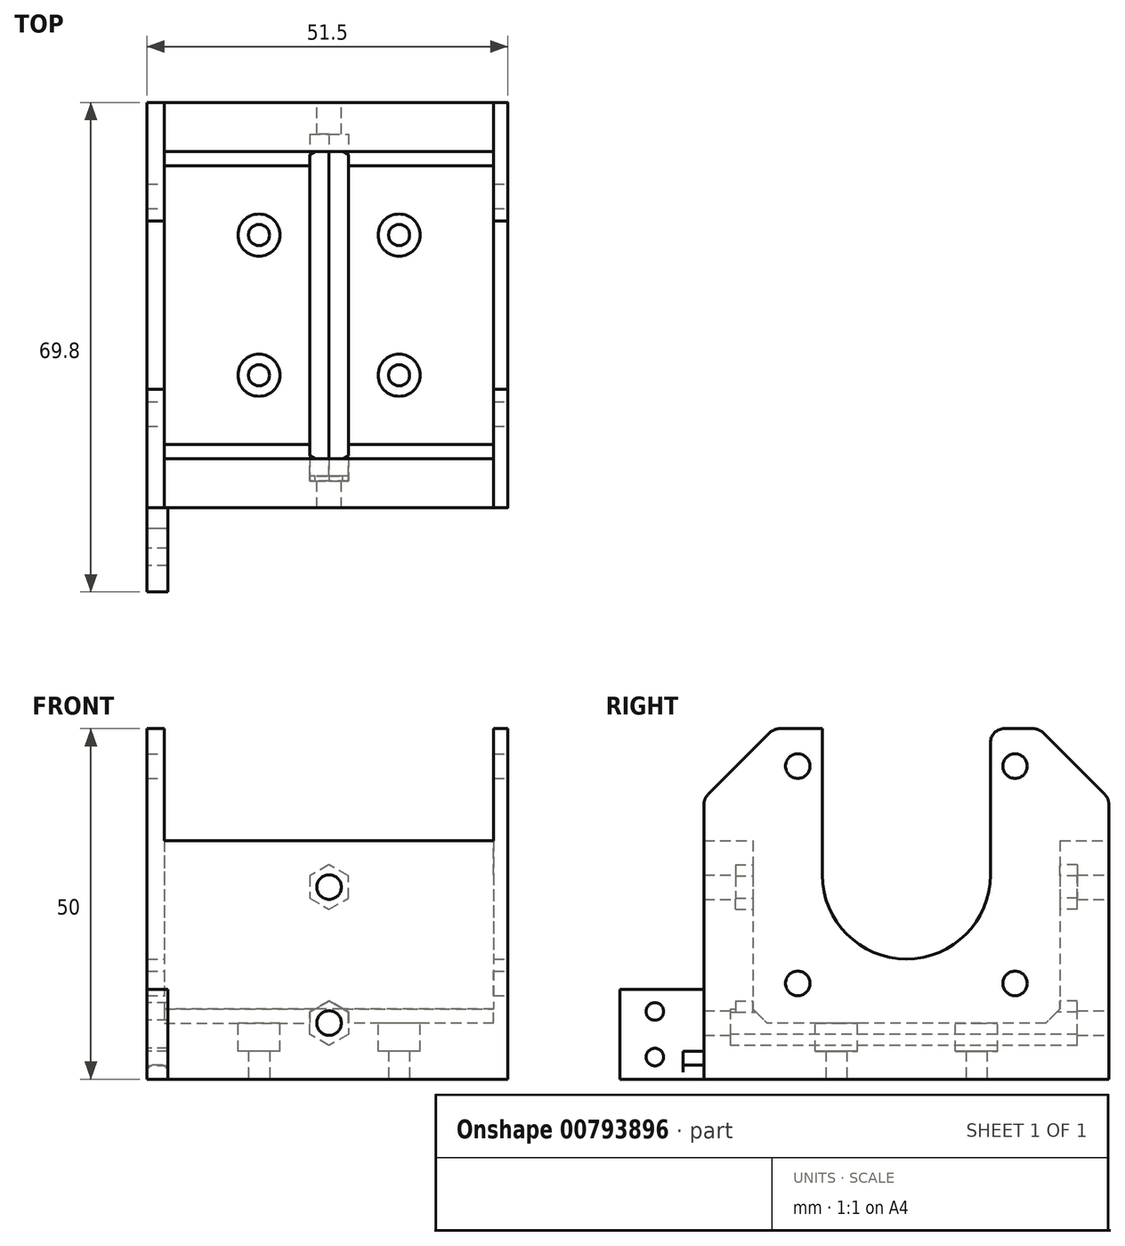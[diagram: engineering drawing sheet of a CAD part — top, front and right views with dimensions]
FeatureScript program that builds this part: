
annotation { "Feature Type Name" : "Feature", "Feature Type Description" : "" }
export const myFeature = defineFeature(function(context is Context, id is Id, definition is map)
    precondition{}
    {
        {
            var Q0;
            Q0=qCreatedBy(makeId("Top.planeOp"),FACE);
            var sketch = newSketch(context, id + "F0", { "sketchPlane" : qUnion([Q0])});
            skLineSegment(sketch, "E0.bottom", {"start": v(-13.5, 21.9) * mm, "end": v(13.5, 21.9) * mm, "construction": true});
            skLineSegment(sketch, "E0.top", {"start": v(-13.5, -21.9) * mm, "end": v(13.5, -21.9) * mm, "construction": true});
            skLineSegment(sketch, "E0.left", {"start": v(-13.5, 21.9) * mm, "end": v(-13.5, -21.9) * mm, "construction": true});
            skLineSegment(sketch, "E0.right", {"start": v(13.5, 21.9) * mm, "end": v(13.5, -21.9) * mm, "construction": true});
            skCircle(sketch, "E1", {"center": v(-10, 10) * mm, "radius": 1.5 * mm, "construction": true});
            skCircle(sketch, "E2", {"center": v(10, 10) * mm, "radius": 1.5 * mm, "construction": true});
            skCircle(sketch, "E3", {"center": v(10, -10) * mm, "radius": 1.5 * mm, "construction": true});
            skCircle(sketch, "E4", {"center": v(-10, -10) * mm, "radius": 1.5 * mm, "construction": true});
            skSolve(sketch);
        }
        {
            var Q0;
            Q0=qCreatedBy(makeId("Top.planeOp"),FACE);
            var sketch = newSketch(context, id + "F1", { "sketchPlane" : qUnion([Q0])});
            skLineSegment(sketch, "E5.0", {"start": v(-13.5, 21.9) * mm, "end": v(-13.5, -21.9) * mm});
            skLineSegment(sketch, "E6.0", {"start": v(-13.5, 21.9) * mm, "end": v(13.5, 21.9) * mm});
            skLineSegment(sketch, "E7.0", {"start": v(13.5, 21.9) * mm, "end": v(13.5, -21.9) * mm});
            skLineSegment(sketch, "E8.0", {"start": v(-13.5, -21.9) * mm, "end": v(13.5, -21.9) * mm});
            skPoint(sketch, "E9.0", {"position": v(-10, -10) * mm});
            skPoint(sketch, "E10.0", {"position": v(10, -10) * mm});
            skPoint(sketch, "E11.0", {"position": v(10, 10) * mm});
            skCircle(sketch, "E12.0", {"center": v(-10, -10) * mm, "radius": 1.5 * mm});
            skCircle(sketch, "E13.0", {"center": v(10, -10) * mm, "radius": 1.5 * mm});
            skCircle(sketch, "E14.0", {"center": v(10, 10) * mm, "radius": 1.5 * mm});
            skCircle(sketch, "E15.0", {"center": v(-10, 10) * mm, "radius": 1.5 * mm});
            skLineSegment(sketch, "E16.top", {"start": v(-13.5, -28.9) * mm, "end": v(13.5, -28.9) * mm});
            skLineSegment(sketch, "E16.left", {"start": v(-13.5, -21.9) * mm, "end": v(-13.5, -28.9) * mm});
            skLineSegment(sketch, "E16.right", {"start": v(13.5, -21.9) * mm, "end": v(13.5, -28.9) * mm});
            skLineSegment(sketch, "E17.top", {"start": v(-13.5, 28.9) * mm, "end": v(13.5, 28.9) * mm});
            skLineSegment(sketch, "E17.left", {"start": v(-13.5, 21.9) * mm, "end": v(-13.5, 28.9) * mm});
            skLineSegment(sketch, "E17.right", {"start": v(13.5, 21.9) * mm, "end": v(13.5, 28.9) * mm});
            skSolve(sketch);
        }
        {
            var Q0;
            Q0=qSketchRegion(id+"F1",true);
            extrude(context, id + "F2", {"entities" : qUnion([Q0]), "depth" : 34 * mm, "offsetDistance" : 25 * mm});
        }
        {
            var Q0;
            Q0=makeQuery(id+"F2.opExtrude","SWEPT_FACE",FACE,{"disambiguationData":[OSD([sQuery(id+"F1.wireOp",EDGE,"E17.top")])]});
            var sketch = newSketch(context, id + "F3", { "sketchPlane" : qUnion([Q0])});
            skCircle(sketch, "E18", {"center": v(0, 27.4) * mm, "radius": 1.75 * mm});
            skCircle(sketch, "E19", {"center": v(0, 8) * mm, "radius": 1.75 * mm});
            skSolve(sketch);
        }
        {
            var Q0;
            Q0=qSketchRegion(id+"F3",true);
            extrude(context, id + "F4", {"entities" : qUnion([Q0]), "operationType" : NewBodyOperationType.REMOVE, "endBound" : BoundingType.THROUGH_ALL, "oppositeDirection" : true, "depth" : 25 * mm, "offsetDistance" : 25 * mm});
        }
        {
            var Q0;
            Q0=makeQuery(id+"F2.opExtrude","SWEPT_FACE",FACE,{"disambiguationData":[OSD([sQuery(id+"F1.wireOp",EDGE,"E5.0"),sQuery(id+"F1.wireOp",EDGE,"E16.left"),sQuery(id+"F1.wireOp",EDGE,"E17.left")])]});
            var sketch = newSketch(context, id + "F5", { "sketchPlane" : qUnion([Q0])});
            skLineSegment(sketch, "E20.bottom", {"start": v(-21.9, 34) * mm, "end": v(21.9, 34) * mm});
            skLineSegment(sketch, "E20.top", {"start": v(-21.9, 8) * mm, "end": v(21.9, 8) * mm});
            skLineSegment(sketch, "E20.left", {"start": v(-21.9, 34) * mm, "end": v(-21.9, 8) * mm});
            skLineSegment(sketch, "E20.right", {"start": v(21.9, 34) * mm, "end": v(21.9, 8) * mm});
            skSolve(sketch);
        }
        {
            var Q0;
            Q0=qSketchRegion(id+"F5",true);
            extrude(context, id + "F6", {"entities" : qUnion([Q0]), "operationType" : NewBodyOperationType.REMOVE, "endBound" : BoundingType.THROUGH_ALL, "oppositeDirection" : true, "depth" : 25 * mm, "offsetDistance" : 25 * mm});
        }
        {
            var Q0;
            Q0=makeQuery(id+"F2.opExtrude","SWEPT_FACE",FACE,{"disambiguationData":[OSD([sQuery(id+"F1.wireOp",EDGE,"E5.0"),sQuery(id+"F1.wireOp",EDGE,"E16.left"),sQuery(id+"F1.wireOp",EDGE,"E17.left")])]});
            extrude(context, id + "F7", {"entities" : qUnion([Q0]), "operationType" : NewBodyOperationType.ADD, "depth" : 10 * mm, "offsetDistance" : 25 * mm});
        }
        {
            var Q0;
            Q0=makeQuery(id+"F2.opExtrude","SWEPT_FACE",FACE,{"disambiguationData":[OSD([sQuery(id+"F1.wireOp",EDGE,"E7.0"),sQuery(id+"F1.wireOp",EDGE,"E16.right"),sQuery(id+"F1.wireOp",EDGE,"E17.right")])]});
            extrude(context, id + "F8", {"entities" : qUnion([Q0]), "operationType" : NewBodyOperationType.ADD, "depth" : 10 * mm, "offsetDistance" : 25 * mm});
        }
        {
            var Q0;
            {var subQ0=sQuery(id+"F5.wireOp",EDGE,"E20.right");var subQ1=sQuery(id+"F5.wireOp",EDGE,"E20.top");Q0=makeQuery(id+"F8.boolean.opBoolean","MERGE",EDGE,{"derivedFrom":[makeQuery(id+"F7.boolean.opBoolean","MERGE",EDGE,{"derivedFrom":[makeQuery(id+"F6.boolean.opBoolean","COPY",EDGE,{"derivedFrom":makeQuery(id+"F6.opExtrude","SWEPT_EDGE",EDGE,{"disambiguationData":[OSD([subQ1,subQ0])]})}),makeQuery(id+"F7.opExtrude","SWEPT_EDGE",EDGE,{"disambiguationData":[OSD([subQ1,subQ0])]})]}),makeQuery(id+"F8.opExtrude","SWEPT_EDGE",EDGE,{"disambiguationData":[OSD([sQuery(id+"F1.wireOp",EDGE,"E7.0"),sQuery(id+"F1.wireOp",EDGE,"E16.right"),sQuery(id+"F1.wireOp",EDGE,"E17.right"),subQ1,subQ0])]})]});}
            var Q1;
            {var subQ0=sQuery(id+"F5.wireOp",EDGE,"E20.left");var subQ1=sQuery(id+"F5.wireOp",EDGE,"E20.top");Q1=makeQuery(id+"F8.boolean.opBoolean","MERGE",EDGE,{"derivedFrom":[makeQuery(id+"F7.boolean.opBoolean","MERGE",EDGE,{"derivedFrom":[makeQuery(id+"F6.boolean.opBoolean","COPY",EDGE,{"derivedFrom":makeQuery(id+"F6.opExtrude","SWEPT_EDGE",EDGE,{"disambiguationData":[OSD([subQ1,subQ0])]})}),makeQuery(id+"F7.opExtrude","SWEPT_EDGE",EDGE,{"disambiguationData":[OSD([subQ1,subQ0])]})]}),makeQuery(id+"F8.opExtrude","SWEPT_EDGE",EDGE,{"disambiguationData":[OSD([sQuery(id+"F1.wireOp",EDGE,"E7.0"),sQuery(id+"F1.wireOp",EDGE,"E16.right"),sQuery(id+"F1.wireOp",EDGE,"E17.right"),subQ1,subQ0])]})]});}
            chamfer(context, id + "F9", {"entities" : qUnion([Q0, Q1]), "width" : 2 * mm, "tangentPropagation" : true});
        }
        {
            var Q0;
            Q0=makeQuery(id+"F7.opExtrude","CAP_FACE",FACE,{"disambiguationData":[OSD([sQuery(id+"F1.wireOp",EDGE,"E5.0"),sQuery(id+"F1.wireOp",EDGE,"E16.left"),sQuery(id+"F1.wireOp",EDGE,"E17.left")])],"isStart":false});
            var sketch = newSketch(context, id + "F10", { "sketchPlane" : qUnion([Q0])});
            skLineSegment(sketch, "E21.0", {"start": v(-21.9, 34) * mm, "end": v(-21.9, 10) * mm});
            skLineSegment(sketch, "E22.0", {"start": v(21.9, 34) * mm, "end": v(21.9, 10) * mm});
            skSolve(sketch);
        }
        {
            var Q0;
            Q0=makeQuery(id+"F10.imprint","IMPRINT",FACE,{"disambiguationData":[TD([[makeQuery(id+"F10.imprint","IMPRINT",EDGE,{"derivedFrom":sQuery(id+"F10.wireOp",EDGE,"E21.0")}),-1.0]])]});
            var sketch = newSketch(context, id + "F11", { "sketchPlane" : qUnion([Q0])});
            skLineSegment(sketch, "E23.0", {"start": v(-28.9, 34) * mm, "end": v(-28.9, 0) * mm});
            skLineSegment(sketch, "E24.0", {"start": v(-28.9, 0) * mm, "end": v(28.9, 0) * mm});
            skLineSegment(sketch, "E25.top", {"start": v(-28.9, 50) * mm, "end": v(28.9, 50) * mm});
            skLineSegment(sketch, "E25.left", {"start": v(-28.9, 34) * mm, "end": v(-28.9, 50) * mm});
            skLineSegment(sketch, "E26", {"start": v(28.9, 50) * mm, "end": v(28.9, 0) * mm});
            skSolve(sketch);
        }
        {
            var Q0;
            Q0=qSketchRegion(id+"F11",true);
            extrude(context, id + "F12", {"entities" : qUnion([Q0]), "operationType" : NewBodyOperationType.ADD, "depth" : 2.5 * mm, "offsetDistance" : 25 * mm});
        }
        {
            var Q0;
            Q0=makeQuery(id+"F8.opExtrude","CAP_FACE",FACE,{"disambiguationData":[OSD([sQuery(id+"F1.wireOp",EDGE,"E7.0"),sQuery(id+"F1.wireOp",EDGE,"E16.right"),sQuery(id+"F1.wireOp",EDGE,"E17.right")])],"isStart":false});
            var sketch = newSketch(context, id + "F13", { "sketchPlane" : qUnion([Q0])});
            skLineSegment(sketch, "E27.0", {"start": v(-28.9, 28) * mm, "end": v(-28.9, 50) * mm});
            skLineSegment(sketch, "E28.0", {"start": v(-28.9, 50) * mm, "end": v(28.9, 50) * mm});
            skLineSegment(sketch, "E29.0", {"start": v(28.9, 28) * mm, "end": v(28.9, 50) * mm});
            skLineSegment(sketch, "E30.0", {"start": v(-28.9, 34) * mm, "end": v(-28.9, 0) * mm});
            skLineSegment(sketch, "E31.0", {"start": v(28.9, 0) * mm, "end": v(-28.9, 0) * mm});
            skLineSegment(sketch, "E32.0", {"start": v(28.9, 34) * mm, "end": v(28.9, 0) * mm});
            skSolve(sketch);
        }
        {
            var Q0;
            Q0=qSketchRegion(id+"F13",true);
            extrude(context, id + "F14", {"entities" : qUnion([Q0]), "operationType" : NewBodyOperationType.ADD, "depth" : 2 * mm, "offsetDistance" : 25 * mm});
        }
        {
            var Q0;
            Q0=makeQuery(id+"F12.opExtrude","SWEPT_EDGE",EDGE,{"disambiguationData":[OSD([sQuery(id+"F11.wireOp",EDGE,"E25.top"),sQuery(id+"F11.wireOp",EDGE,"E25.left")])]});
            var Q1;
            Q1=makeQuery(id+"F12.opExtrude","SWEPT_EDGE",EDGE,{"disambiguationData":[OSD([sQuery(id+"F11.wireOp",EDGE,"E25.top"),sQuery(id+"F11.wireOp",EDGE,"E26")])]});
            var Q2;
            Q2=makeQuery(id+"F14.opExtrude","SWEPT_EDGE",EDGE,{"disambiguationData":[OSD([sQuery(id+"F13.wireOp",EDGE,"E27.0"),sQuery(id+"F13.wireOp",EDGE,"E28.0")])]});
            var Q3;
            Q3=makeQuery(id+"F14.opExtrude","SWEPT_EDGE",EDGE,{"disambiguationData":[OSD([sQuery(id+"F13.wireOp",EDGE,"E28.0"),sQuery(id+"F13.wireOp",EDGE,"E29.0")])]});
            chamfer(context, id + "F15", {"entities" : qUnion([Q0, Q1, Q2, Q3]), "width" : 10 * mm, "tangentPropagation" : true});
        }
        {
            var Q0;
            Q0=makeQuery(id+"F14.opExtrude","CAP_FACE",FACE,{"disambiguationData":[OSD([sQuery(id+"F13.wireOp",EDGE,"E27.0"),sQuery(id+"F13.wireOp",EDGE,"E28.0"),sQuery(id+"F13.wireOp",EDGE,"E29.0"),sQuery(id+"F13.wireOp",EDGE,"E30.0"),sQuery(id+"F13.wireOp",EDGE,"E31.0"),sQuery(id+"F13.wireOp",EDGE,"E32.0")])],"isStart":false});
            var sketch = newSketch(context, id + "F16", { "sketchPlane" : qUnion([Q0])});
            skArc(sketch, "E33", {"start": v(-12, 29.15) * mm, "mid": v(0, 17.15) * mm, "end": v(12, 29.15) * mm});
            skCircle(sketch, "E34", {"center": v(-15.5, 44.65) * mm, "radius": 1.75 * mm});
            skCircle(sketch, "E35", {"center": v(15.5, 44.65) * mm, "radius": 1.75 * mm});
            skCircle(sketch, "E36", {"center": v(15.5, 13.65) * mm, "radius": 1.75 * mm});
            skCircle(sketch, "E37", {"center": v(-15.5, 13.65) * mm, "radius": 1.75 * mm});
            skLineSegment(sketch, "E38", {"start": v(-12, 29.15) * mm, "end": v(-12, 50) * mm});
            skLineSegment(sketch, "E39", {"start": v(12, 29.15) * mm, "end": v(12, 50) * mm});
            skLineSegment(sketch, "E40", {"start": v(-12, 50) * mm, "end": v(12, 50) * mm});
            skSolve(sketch);
        }
        {
            var Q0;
            Q0=qSketchRegion(id+"F16",true);
            var Q1;
            Q1=makeQuery(id+"F12.opExtrude","CAP_FACE",FACE,{"disambiguationData":[OSD([sQuery(id+"F11.wireOp",EDGE,"E23.0"),sQuery(id+"F11.wireOp",EDGE,"E24.0"),sQuery(id+"F11.wireOp",EDGE,"E25.top"),sQuery(id+"F11.wireOp",EDGE,"E25.left"),sQuery(id+"F11.wireOp",EDGE,"E26")])],"isStart":false});
            extrude(context, id + "F17", {"entities" : qUnion([Q0]), "operationType" : NewBodyOperationType.REMOVE, "endBound" : BoundingType.UP_TO_SURFACE, "oppositeDirection" : true, "depth" : 25 * mm, "endBoundEntityFace" : qUnion([Q1]), "offsetDistance" : 25 * mm});
        }
        {
            var Q0;
            {var subQ0=sQuery(id+"F5.wireOp",EDGE,"E20.top");Q0=makeQuery(id+"F8.boolean.opBoolean","MERGE",FACE,{"derivedFrom":[makeQuery(id+"F7.boolean.opBoolean","MERGE",FACE,{"derivedFrom":[makeQuery(id+"F6.boolean.opBoolean","COPY",FACE,{"derivedFrom":makeQuery(id+"F6.opExtrude","SWEPT_FACE",FACE,{"disambiguationData":[OSD([subQ0])]})}),makeQuery(id+"F7.opExtrude","SWEPT_FACE",FACE,{"disambiguationData":[OSD([subQ0])]})]}),makeQuery(id+"F8.opExtrude","SWEPT_FACE",FACE,{"disambiguationData":[OSD([sQuery(id+"F1.wireOp",EDGE,"E7.0"),sQuery(id+"F1.wireOp",EDGE,"E16.right"),sQuery(id+"F1.wireOp",EDGE,"E17.right"),subQ0])]})]});}
            var sketch = newSketch(context, id + "F18", { "sketchPlane" : qUnion([Q0])});
            skPoint(sketch, "E41", {"position": v(10, -10) * mm});
            skPoint(sketch, "E42", {"position": v(10, 10) * mm});
            skCircle(sketch, "E43", {"center": v(10, -10) * mm, "radius": 3 * mm});
            skCircle(sketch, "E44", {"center": v(10, 10) * mm, "radius": 3 * mm});
            skCircle(sketch, "E45.0", {"center": v(-10, -10) * mm, "radius": 1.5 * mm, "construction": true});
            skCircle(sketch, "E46.0", {"center": v(-10, 10) * mm, "radius": 1.5 * mm, "construction": true});
            skCircle(sketch, "E47", {"center": v(-10, -10) * mm, "radius": 3 * mm});
            skCircle(sketch, "E48", {"center": v(-10, 10) * mm, "radius": 3 * mm});
            skSolve(sketch);
        }
        {
            var Q0;
            Q0=qSketchRegion(id+"F18",true);
            extrude(context, id + "F19", {"entities" : qUnion([Q0]), "operationType" : NewBodyOperationType.REMOVE, "oppositeDirection" : true, "depth" : 4 * mm, "offsetDistance" : 25 * mm});
        }
        {
            var Q0;
            {var subQ0=sQuery(id+"F5.wireOp",EDGE,"E20.left");Q0=makeQuery(id+"F8.boolean.opBoolean","MERGE",FACE,{"derivedFrom":[makeQuery(id+"F7.boolean.opBoolean","MERGE",FACE,{"derivedFrom":[makeQuery(id+"F6.boolean.opBoolean","COPY",FACE,{"derivedFrom":makeQuery(id+"F6.opExtrude","SWEPT_FACE",FACE,{"disambiguationData":[OSD([subQ0])]})}),makeQuery(id+"F7.opExtrude","SWEPT_FACE",FACE,{"disambiguationData":[OSD([subQ0])]})]}),makeQuery(id+"F8.opExtrude","SWEPT_FACE",FACE,{"disambiguationData":[OSD([sQuery(id+"F1.wireOp",EDGE,"E7.0"),sQuery(id+"F1.wireOp",EDGE,"E16.right"),sQuery(id+"F1.wireOp",EDGE,"E17.right"),subQ0])]})]});}
            var sketch = newSketch(context, id + "F20", { "sketchPlane" : qUnion([Q0])});
            skPoint(sketch, "E49", {"position": v(0, 25.64) * mm});
            skPoint(sketch, "E50", {"position": v(0, 27.4) * mm});
            skPoint(sketch, "E51", {"position": v(0, 7.96) * mm});
            skPoint(sketch, "E51.positionSnap0", {"position": v(0, 10) * mm});
            skCircle(sketch, "E52.cCircle", {"center": v(0, 27.4) * mm, "radius": 2.75 * mm, "construction": true});
            skLineSegment(sketch, "E52.0", {"start": v(2.75, 28.98) * mm, "end": v(2.75, 25.8) * mm});
            skLineSegment(sketch, "E52.1", {"start": v(2.75, 25.8) * mm, "end": v(0, 24.22) * mm});
            skLineSegment(sketch, "E52.2", {"start": v(0, 24.22) * mm, "end": v(-2.75, 25.8) * mm});
            skLineSegment(sketch, "E52.3", {"start": v(-2.75, 25.8) * mm, "end": v(-2.75, 28.98) * mm});
            skLineSegment(sketch, "E52.4", {"start": v(-2.75, 28.98) * mm, "end": v(0, 30.57) * mm});
            skLineSegment(sketch, "E52.5", {"start": v(0, 30.57) * mm, "end": v(2.75, 28.98) * mm});
            skPoint(sketch, "E52.0.midPoint", {"position": v(2.75, 27.4) * mm});
            skCircle(sketch, "E53.cCircle", {"center": v(0, 7.96) * mm, "radius": 2.75 * mm, "construction": true});
            skLineSegment(sketch, "E53.0", {"start": v(2.75, 9.55) * mm, "end": v(2.75, 6.38) * mm});
            skLineSegment(sketch, "E53.1", {"start": v(2.75, 6.38) * mm, "end": v(0, 4.79) * mm});
            skLineSegment(sketch, "E53.2", {"start": v(0, 4.79) * mm, "end": v(-2.75, 6.38) * mm});
            skLineSegment(sketch, "E53.3", {"start": v(-2.75, 6.38) * mm, "end": v(-2.75, 9.55) * mm});
            skLineSegment(sketch, "E53.4", {"start": v(-2.75, 9.55) * mm, "end": v(0, 11.14) * mm});
            skLineSegment(sketch, "E53.5", {"start": v(0, 11.14) * mm, "end": v(2.75, 9.55) * mm});
            skPoint(sketch, "E53.0.midPoint", {"position": v(2.75, 7.96) * mm});
            skSolve(sketch);
        }
        {
            var Q0;
            Q0=qSketchRegion(id+"F20",true);
            extrude(context, id + "F21", {"entities" : qUnion([Q0]), "operationType" : NewBodyOperationType.REMOVE, "oppositeDirection" : true, "depth" : 2.5 * mm, "offsetDistance" : 25 * mm});
        }
        {
            var Q0;
            {var subQ12=sQuery(id+"F20.wireOp",EDGE,"E53.0");Q0=makeQuery(id+"F20.imprint","IMPRINT",FACE,{"disambiguationData":[TD([[makeQuery(id+"F20.imprint","IMPRINT",EDGE,{"derivedFrom":subQ12}),-1.0]])]});}
            extrude(context, id + "F22", {"entities" : qUnion([Q0]), "operationType" : NewBodyOperationType.REMOVE, "depth" : 47 * mm, "offsetDistance" : 25 * mm});
        }
        {
            var Q0;
            {var subQ0=sQuery(id+"F5.wireOp",EDGE,"E20.right");Q0=makeQuery(id+"F8.boolean.opBoolean","MERGE",FACE,{"derivedFrom":[makeQuery(id+"F7.boolean.opBoolean","MERGE",FACE,{"derivedFrom":[makeQuery(id+"F6.boolean.opBoolean","COPY",FACE,{"derivedFrom":makeQuery(id+"F6.opExtrude","SWEPT_FACE",FACE,{"disambiguationData":[OSD([subQ0])]})}),makeQuery(id+"F7.opExtrude","SWEPT_FACE",FACE,{"disambiguationData":[OSD([subQ0])]})]}),makeQuery(id+"F8.opExtrude","SWEPT_FACE",FACE,{"disambiguationData":[OSD([sQuery(id+"F1.wireOp",EDGE,"E7.0"),sQuery(id+"F1.wireOp",EDGE,"E16.right"),sQuery(id+"F1.wireOp",EDGE,"E17.right"),subQ0])]})]});}
            var sketch = newSketch(context, id + "F23", { "sketchPlane" : qUnion([Q0])});
            skCircle(sketch, "E54.0", {"center": v(0, 27.4) * mm, "radius": 1.75 * mm, "construction": true});
            skCircle(sketch, "E55.0", {"center": v(0, 8) * mm, "radius": 1.75 * mm, "construction": true});
            skCircle(sketch, "E56.cCircle", {"center": v(0, 27.4) * mm, "radius": 2.75 * mm, "construction": true});
            skLineSegment(sketch, "E56.0", {"start": v(2.75, 28.98) * mm, "end": v(2.75, 25.8) * mm});
            skLineSegment(sketch, "E56.1", {"start": v(2.75, 25.8) * mm, "end": v(0, 24.22) * mm});
            skLineSegment(sketch, "E56.2", {"start": v(0, 24.22) * mm, "end": v(-2.75, 25.8) * mm});
            skLineSegment(sketch, "E56.3", {"start": v(-2.75, 25.8) * mm, "end": v(-2.75, 28.98) * mm});
            skLineSegment(sketch, "E56.4", {"start": v(-2.75, 28.98) * mm, "end": v(0, 30.57) * mm});
            skLineSegment(sketch, "E56.5", {"start": v(0, 30.57) * mm, "end": v(2.75, 28.98) * mm});
            skPoint(sketch, "E56.0.midPoint", {"position": v(2.75, 27.4) * mm});
            skCircle(sketch, "E57.cCircle", {"center": v(0, 8) * mm, "radius": 2.75 * mm, "construction": true});
            skLineSegment(sketch, "E57.0", {"start": v(2.75, 9.59) * mm, "end": v(2.75, 6.41) * mm});
            skLineSegment(sketch, "E57.1", {"start": v(2.75, 6.41) * mm, "end": v(0, 4.82) * mm});
            skLineSegment(sketch, "E57.2", {"start": v(0, 4.82) * mm, "end": v(-2.75, 6.41) * mm});
            skLineSegment(sketch, "E57.3", {"start": v(-2.75, 6.41) * mm, "end": v(-2.75, 9.59) * mm});
            skLineSegment(sketch, "E57.4", {"start": v(-2.75, 9.59) * mm, "end": v(0, 11.18) * mm});
            skLineSegment(sketch, "E57.5", {"start": v(0, 11.18) * mm, "end": v(2.75, 9.59) * mm});
            skPoint(sketch, "E57.0.midPoint", {"position": v(2.75, 8) * mm});
            skSolve(sketch);
        }
        {
            var Q0;
            Q0=qSketchRegion(id+"F23",true);
            extrude(context, id + "F24", {"entities" : qUnion([Q0]), "operationType" : NewBodyOperationType.REMOVE, "oppositeDirection" : true, "depth" : 2.5 * mm, "offsetDistance" : 25 * mm});
        }
        {
            var Q0;
            Q0=makeQuery(id+"F12.opExtrude","CAP_FACE",FACE,{"disambiguationData":[OSD([sQuery(id+"F11.wireOp",EDGE,"E23.0"),sQuery(id+"F11.wireOp",EDGE,"E24.0"),sQuery(id+"F11.wireOp",EDGE,"E25.top"),sQuery(id+"F11.wireOp",EDGE,"E25.left"),sQuery(id+"F11.wireOp",EDGE,"E26")])],"isStart":false});
            var sketch = newSketch(context, id + "F25", { "sketchPlane" : qUnion([Q0])});
            skLineSegment(sketch, "E58.bottom", {"start": v(28.9, 0) * mm, "end": v(40.9, 0) * mm});
            skLineSegment(sketch, "E58.top", {"start": v(28.9, 12.8) * mm, "end": v(40.9, 12.8) * mm});
            skLineSegment(sketch, "E58.left", {"start": v(28.9, 0) * mm, "end": v(28.9, 2) * mm});
            skLineSegment(sketch, "E58.right", {"start": v(40.9, 0) * mm, "end": v(40.9, 12.8) * mm});
            skCircle(sketch, "E59", {"center": v(35.9, 9.65) * mm, "radius": 1.25 * mm});
            skCircle(sketch, "E60", {"center": v(35.9, 3.15) * mm, "radius": 1.25 * mm});
            skPoint(sketch, "E61", {"position": v(40.9, 6.4) * mm});
            skLineSegment(sketch, "E62.bottom", {"start": v(28.9, 2) * mm, "end": v(31.9, 2) * mm});
            skLineSegment(sketch, "E62.top", {"start": v(28.9, 4) * mm, "end": v(31.9, 4) * mm});
            skLineSegment(sketch, "E62.right", {"start": v(31.9, 2) * mm, "end": v(31.9, 4) * mm});
            skLineSegment(sketch, "E63.trimOffspring", {"start": v(28.9, 4) * mm, "end": v(28.9, 12.8) * mm});
            skSolve(sketch);
        }
        {
            var Q0;
            Q0=qSketchRegion(id+"F25",true);
            extrude(context, id + "F26", {"entities" : qUnion([Q0]), "operationType" : NewBodyOperationType.ADD, "oppositeDirection" : true, "depth" : 3 * mm, "offsetDistance" : 25 * mm});
        }
        {
            var Q0;
            Q0=makeQuery(id+"F26.opExtrude","SWEPT_EDGE",EDGE,{"disambiguationData":[OSD([sQuery(id+"F11.wireOp",EDGE,"E26"),sQuery(id+"F25.wireOp",EDGE,"E58.top"),sQuery(id+"F25.wireOp",EDGE,"E63.trimOffspring")])]});
            var Q1;
            {var subQ0=sQuery(id+"F1.wireOp",EDGE,"E17.right");var subQ1=sQuery(id+"F1.wireOp",EDGE,"E16.right");var subQ2=sQuery(id+"F1.wireOp",EDGE,"E16.top");var subQ3=sQuery(id+"F1.wireOp",EDGE,"E7.0");Q1=makeQuery(id+"F8.opExtrude","CAP_EDGE",EDGE,{"disambiguationData":[OSD([subQ3,subQ1,subQ0]),TDD([makeQuery(id+"F6.boolean.opBoolean","SPLIT",EDGE,{"disambiguationData":[TD([makeQuery(id+"F2.opExtrude","SWEPT_FACE",FACE,{"disambiguationData":[OSD([subQ2])]})])],"derivedFrom":makeQuery(id+"F2.opExtrude","CAP_EDGE",EDGE,{"disambiguationData":[OSD([subQ3,subQ1,subQ0])],"isStart":false})})])],"isStart":false});}
            var Q2;
            {var subQ0=sQuery(id+"F1.wireOp",EDGE,"E17.left");var subQ1=sQuery(id+"F1.wireOp",EDGE,"E16.left");var subQ2=sQuery(id+"F1.wireOp",EDGE,"E16.top");var subQ3=sQuery(id+"F1.wireOp",EDGE,"E5.0");Q2=makeQuery(id+"F7.opExtrude","CAP_EDGE",EDGE,{"disambiguationData":[OSD([subQ3,subQ1,subQ0]),TDD([makeQuery(id+"F6.boolean.opBoolean","SPLIT",EDGE,{"disambiguationData":[TD([makeQuery(id+"F2.opExtrude","SWEPT_FACE",FACE,{"disambiguationData":[OSD([subQ2])]})])],"derivedFrom":makeQuery(id+"F2.opExtrude","CAP_EDGE",EDGE,{"disambiguationData":[OSD([subQ3,subQ1,subQ0])],"isStart":false})})])],"isStart":false});}
            var Q3;
            {var subQ0=sQuery(id+"F1.wireOp",EDGE,"E17.left");var subQ1=sQuery(id+"F1.wireOp",EDGE,"E17.top");var subQ2=sQuery(id+"F1.wireOp",EDGE,"E16.left");var subQ3=sQuery(id+"F1.wireOp",EDGE,"E5.0");Q3=makeQuery(id+"F7.opExtrude","CAP_EDGE",EDGE,{"disambiguationData":[OSD([subQ3,subQ2,subQ0]),TDD([makeQuery(id+"F6.boolean.opBoolean","SPLIT",EDGE,{"disambiguationData":[TD([makeQuery(id+"F2.opExtrude","SWEPT_FACE",FACE,{"disambiguationData":[OSD([subQ1])]})])],"derivedFrom":makeQuery(id+"F2.opExtrude","CAP_EDGE",EDGE,{"disambiguationData":[OSD([subQ3,subQ2,subQ0])],"isStart":false})})])],"isStart":false});}
            var Q4;
            {var subQ0=sQuery(id+"F1.wireOp",EDGE,"E17.right");var subQ1=sQuery(id+"F1.wireOp",EDGE,"E17.top");var subQ2=sQuery(id+"F1.wireOp",EDGE,"E16.right");var subQ3=sQuery(id+"F1.wireOp",EDGE,"E7.0");Q4=makeQuery(id+"F8.opExtrude","CAP_EDGE",EDGE,{"disambiguationData":[OSD([subQ3,subQ2,subQ0]),TDD([makeQuery(id+"F6.boolean.opBoolean","SPLIT",EDGE,{"disambiguationData":[TD([makeQuery(id+"F2.opExtrude","SWEPT_FACE",FACE,{"disambiguationData":[OSD([subQ1])]})])],"derivedFrom":makeQuery(id+"F2.opExtrude","CAP_EDGE",EDGE,{"disambiguationData":[OSD([subQ3,subQ2,subQ0])],"isStart":false})})])],"isStart":false});}
            var Q5;
            Q5=makeQuery(id+"F26.opExtrude","CAP_EDGE",EDGE,{"disambiguationData":[OSD([sQuery(id+"F25.wireOp",EDGE,"E63.trimOffspring")])],"isStart":false});
            var Q6;
            Q6=makeQuery(id+"F26.opExtrude","CAP_EDGE",EDGE,{"disambiguationData":[OSD([sQuery(id+"F25.wireOp",EDGE,"E58.left")])],"isStart":false});
            var Q7;
            {var subQ0=sQuery(id+"F13.wireOp",EDGE,"E29.0");var subQ1=sQuery(id+"F1.wireOp",EDGE,"E17.top");Q7=makeQuery(id+"F15.opChamfer","BLEND_EDGE",EDGE,{"blendedFrom":[makeQuery(id+"F14.opExtrude","SWEPT_EDGE",EDGE,{"disambiguationData":[OSD([sQuery(id+"F13.wireOp",EDGE,"E28.0"),subQ0])]}),makeQuery(id+"F14.boolean.opBoolean","MERGE",FACE,{"derivedFrom":[makeQuery(id+"F12.boolean.opBoolean","MERGE",FACE,{"derivedFrom":[makeQuery(id+"F8.boolean.opBoolean","MERGE",FACE,{"derivedFrom":[makeQuery(id+"F7.boolean.opBoolean","MERGE",FACE,{"derivedFrom":[makeQuery(id+"F2.opExtrude","SWEPT_FACE",FACE,{"disambiguationData":[OSD([subQ1])]}),makeQuery(id+"F7.opExtrude","SWEPT_FACE",FACE,{"disambiguationData":[OSD([subQ1,sQuery(id+"F1.wireOp",EDGE,"E17.left")])]})]}),makeQuery(id+"F8.opExtrude","SWEPT_FACE",FACE,{"disambiguationData":[OSD([subQ1,sQuery(id+"F1.wireOp",EDGE,"E17.right")])]})]}),makeQuery(id+"F12.opExtrude","SWEPT_FACE",FACE,{"disambiguationData":[OSD([sQuery(id+"F11.wireOp",EDGE,"E23.0"),sQuery(id+"F11.wireOp",EDGE,"E25.left")])]})]}),makeQuery(id+"F14.opExtrude","SWEPT_FACE",FACE,{"disambiguationData":[OSD([subQ0,sQuery(id+"F13.wireOp",EDGE,"E32.0")])]})]})],"blendedInto":[makeQuery(id+"F14.boolean.opBoolean","MERGE",FACE,{"derivedFrom":[makeQuery(id+"F12.boolean.opBoolean","MERGE",FACE,{"derivedFrom":[makeQuery(id+"F8.boolean.opBoolean","MERGE",FACE,{"derivedFrom":[makeQuery(id+"F7.boolean.opBoolean","MERGE",FACE,{"derivedFrom":[makeQuery(id+"F2.opExtrude","SWEPT_FACE",FACE,{"disambiguationData":[OSD([subQ1])]}),makeQuery(id+"F7.opExtrude","SWEPT_FACE",FACE,{"disambiguationData":[OSD([subQ1,sQuery(id+"F1.wireOp",EDGE,"E17.left")])]})]}),makeQuery(id+"F8.opExtrude","SWEPT_FACE",FACE,{"disambiguationData":[OSD([subQ1,sQuery(id+"F1.wireOp",EDGE,"E17.right")])]})]}),makeQuery(id+"F12.opExtrude","SWEPT_FACE",FACE,{"disambiguationData":[OSD([sQuery(id+"F11.wireOp",EDGE,"E23.0"),sQuery(id+"F11.wireOp",EDGE,"E25.left")])]})]}),makeQuery(id+"F14.opExtrude","SWEPT_FACE",FACE,{"disambiguationData":[OSD([subQ0,sQuery(id+"F13.wireOp",EDGE,"E32.0")])]})]})]});}
            var Q8;
            {var subQ0=sQuery(id+"F11.wireOp",EDGE,"E25.left");var subQ1=sQuery(id+"F1.wireOp",EDGE,"E17.top");Q8=makeQuery(id+"F15.opChamfer","BLEND_EDGE",EDGE,{"blendedFrom":[makeQuery(id+"F12.opExtrude","SWEPT_EDGE",EDGE,{"disambiguationData":[OSD([sQuery(id+"F11.wireOp",EDGE,"E25.top"),subQ0])]}),makeQuery(id+"F14.boolean.opBoolean","MERGE",FACE,{"derivedFrom":[makeQuery(id+"F12.boolean.opBoolean","MERGE",FACE,{"derivedFrom":[makeQuery(id+"F8.boolean.opBoolean","MERGE",FACE,{"derivedFrom":[makeQuery(id+"F7.boolean.opBoolean","MERGE",FACE,{"derivedFrom":[makeQuery(id+"F2.opExtrude","SWEPT_FACE",FACE,{"disambiguationData":[OSD([subQ1])]}),makeQuery(id+"F7.opExtrude","SWEPT_FACE",FACE,{"disambiguationData":[OSD([subQ1,sQuery(id+"F1.wireOp",EDGE,"E17.left")])]})]}),makeQuery(id+"F8.opExtrude","SWEPT_FACE",FACE,{"disambiguationData":[OSD([subQ1,sQuery(id+"F1.wireOp",EDGE,"E17.right")])]})]}),makeQuery(id+"F12.opExtrude","SWEPT_FACE",FACE,{"disambiguationData":[OSD([sQuery(id+"F11.wireOp",EDGE,"E23.0"),subQ0])]})]}),makeQuery(id+"F14.opExtrude","SWEPT_FACE",FACE,{"disambiguationData":[OSD([sQuery(id+"F13.wireOp",EDGE,"E29.0"),sQuery(id+"F13.wireOp",EDGE,"E32.0")])]})]})],"blendedInto":[makeQuery(id+"F14.boolean.opBoolean","MERGE",FACE,{"derivedFrom":[makeQuery(id+"F12.boolean.opBoolean","MERGE",FACE,{"derivedFrom":[makeQuery(id+"F8.boolean.opBoolean","MERGE",FACE,{"derivedFrom":[makeQuery(id+"F7.boolean.opBoolean","MERGE",FACE,{"derivedFrom":[makeQuery(id+"F2.opExtrude","SWEPT_FACE",FACE,{"disambiguationData":[OSD([subQ1])]}),makeQuery(id+"F7.opExtrude","SWEPT_FACE",FACE,{"disambiguationData":[OSD([subQ1,sQuery(id+"F1.wireOp",EDGE,"E17.left")])]})]}),makeQuery(id+"F8.opExtrude","SWEPT_FACE",FACE,{"disambiguationData":[OSD([subQ1,sQuery(id+"F1.wireOp",EDGE,"E17.right")])]})]}),makeQuery(id+"F12.opExtrude","SWEPT_FACE",FACE,{"disambiguationData":[OSD([sQuery(id+"F11.wireOp",EDGE,"E23.0"),subQ0])]})]}),makeQuery(id+"F14.opExtrude","SWEPT_FACE",FACE,{"disambiguationData":[OSD([sQuery(id+"F13.wireOp",EDGE,"E29.0"),sQuery(id+"F13.wireOp",EDGE,"E32.0")])]})]})]});}
            var Q9;
            {var subQ0=sQuery(id+"F11.wireOp",EDGE,"E25.top");Q9=makeQuery(id+"F15.opChamfer","BLEND_EDGE",EDGE,{"blendedFrom":[makeQuery(id+"F12.opExtrude","SWEPT_EDGE",EDGE,{"disambiguationData":[OSD([subQ0,sQuery(id+"F11.wireOp",EDGE,"E25.left")])]}),makeQuery(id+"F12.opExtrude","SWEPT_FACE",FACE,{"disambiguationData":[OSD([subQ0])]})],"blendedInto":[makeQuery(id+"F12.opExtrude","SWEPT_FACE",FACE,{"disambiguationData":[OSD([subQ0])]})]});}
            var Q10;
            {var subQ0=sQuery(id+"F16.wireOp",EDGE,"E38");Q10=makeQuery(id+"F17.boolean.opBoolean","COPY",EDGE,{"disambiguationData":[topologyDisambiguationEdgeConnected([makeQuery(id+"F12.opExtrude","SWEPT_FACE",FACE,{"disambiguationData":[OSD([sQuery(id+"F11.wireOp",EDGE,"E25.top")])]})])],"derivedFrom":makeQuery(id+"F17.opExtrude","SWEPT_EDGE",EDGE,{"disambiguationData":[OSD([sQuery(id+"F13.wireOp",EDGE,"E28.0"),subQ0,sQuery(id+"F16.wireOp",EDGE,"E40")])]})});}
            var Q11;
            {var subQ0=sQuery(id+"F16.wireOp",EDGE,"E39");Q11=makeQuery(id+"F17.boolean.opBoolean","COPY",EDGE,{"disambiguationData":[topologyDisambiguationEdgeConnected([makeQuery(id+"F12.opExtrude","SWEPT_FACE",FACE,{"disambiguationData":[OSD([sQuery(id+"F11.wireOp",EDGE,"E25.top")])]})])],"derivedFrom":makeQuery(id+"F17.opExtrude","SWEPT_EDGE",EDGE,{"disambiguationData":[OSD([sQuery(id+"F13.wireOp",EDGE,"E28.0"),subQ0,sQuery(id+"F16.wireOp",EDGE,"E40")])]})});}
            var Q12;
            {var subQ0=sQuery(id+"F11.wireOp",EDGE,"E25.top");Q12=makeQuery(id+"F15.opChamfer","BLEND_EDGE",EDGE,{"blendedFrom":[makeQuery(id+"F12.opExtrude","SWEPT_EDGE",EDGE,{"disambiguationData":[OSD([subQ0,sQuery(id+"F11.wireOp",EDGE,"E26")])]}),makeQuery(id+"F12.opExtrude","SWEPT_FACE",FACE,{"disambiguationData":[OSD([subQ0])]})],"blendedInto":[makeQuery(id+"F12.opExtrude","SWEPT_FACE",FACE,{"disambiguationData":[OSD([subQ0])]})]});}
            var Q13;
            {var subQ0=sQuery(id+"F13.wireOp",EDGE,"E28.0");var subQ1=sQuery(id+"F16.wireOp",EDGE,"E38");Q13=makeQuery(id+"F17.boolean.opBoolean","COPY",EDGE,{"disambiguationData":[topologyDisambiguationEdgeConnected([makeQuery(id+"F14.opExtrude","SWEPT_FACE",FACE,{"disambiguationData":[OSD([subQ0])]})])],"derivedFrom":makeQuery(id+"F17.opExtrude","SWEPT_EDGE",EDGE,{"disambiguationData":[OSD([subQ0,subQ1,sQuery(id+"F16.wireOp",EDGE,"E40")])]})});}
            var Q14;
            {var subQ0=sQuery(id+"F13.wireOp",EDGE,"E28.0");var subQ1=sQuery(id+"F16.wireOp",EDGE,"E39");Q14=makeQuery(id+"F17.boolean.opBoolean","COPY",EDGE,{"disambiguationData":[topologyDisambiguationEdgeConnected([makeQuery(id+"F14.opExtrude","SWEPT_FACE",FACE,{"disambiguationData":[OSD([subQ0])]})])],"derivedFrom":makeQuery(id+"F17.opExtrude","SWEPT_EDGE",EDGE,{"disambiguationData":[OSD([subQ0,subQ1,sQuery(id+"F16.wireOp",EDGE,"E40")])]})});}
            var Q15;
            {var subQ0=sQuery(id+"F13.wireOp",EDGE,"E28.0");Q15=makeQuery(id+"F15.opChamfer","BLEND_EDGE",EDGE,{"blendedFrom":[makeQuery(id+"F14.opExtrude","SWEPT_EDGE",EDGE,{"disambiguationData":[OSD([sQuery(id+"F13.wireOp",EDGE,"E27.0"),subQ0])]}),makeQuery(id+"F14.opExtrude","SWEPT_FACE",FACE,{"disambiguationData":[OSD([subQ0])]})],"blendedInto":[makeQuery(id+"F14.opExtrude","SWEPT_FACE",FACE,{"disambiguationData":[OSD([subQ0])]})]});}
            var Q16;
            {var subQ0=sQuery(id+"F13.wireOp",EDGE,"E27.0");var subQ1=sQuery(id+"F1.wireOp",EDGE,"E16.top");Q16=makeQuery(id+"F15.opChamfer","BLEND_EDGE",EDGE,{"blendedFrom":[makeQuery(id+"F14.opExtrude","SWEPT_EDGE",EDGE,{"disambiguationData":[OSD([subQ0,sQuery(id+"F13.wireOp",EDGE,"E28.0")])]}),makeQuery(id+"F14.boolean.opBoolean","MERGE",FACE,{"derivedFrom":[makeQuery(id+"F12.boolean.opBoolean","MERGE",FACE,{"derivedFrom":[makeQuery(id+"F8.boolean.opBoolean","MERGE",FACE,{"derivedFrom":[makeQuery(id+"F7.boolean.opBoolean","MERGE",FACE,{"derivedFrom":[makeQuery(id+"F2.opExtrude","SWEPT_FACE",FACE,{"disambiguationData":[OSD([subQ1])]}),makeQuery(id+"F7.opExtrude","SWEPT_FACE",FACE,{"disambiguationData":[OSD([subQ1,sQuery(id+"F1.wireOp",EDGE,"E16.left")])]})]}),makeQuery(id+"F8.opExtrude","SWEPT_FACE",FACE,{"disambiguationData":[OSD([subQ1,sQuery(id+"F1.wireOp",EDGE,"E16.right")])]})]}),makeQuery(id+"F12.opExtrude","SWEPT_FACE",FACE,{"disambiguationData":[OSD([sQuery(id+"F11.wireOp",EDGE,"E26")])]})]}),makeQuery(id+"F14.opExtrude","SWEPT_FACE",FACE,{"disambiguationData":[OSD([subQ0,sQuery(id+"F13.wireOp",EDGE,"E30.0")])]})]})],"blendedInto":[makeQuery(id+"F14.boolean.opBoolean","MERGE",FACE,{"derivedFrom":[makeQuery(id+"F12.boolean.opBoolean","MERGE",FACE,{"derivedFrom":[makeQuery(id+"F8.boolean.opBoolean","MERGE",FACE,{"derivedFrom":[makeQuery(id+"F7.boolean.opBoolean","MERGE",FACE,{"derivedFrom":[makeQuery(id+"F2.opExtrude","SWEPT_FACE",FACE,{"disambiguationData":[OSD([subQ1])]}),makeQuery(id+"F7.opExtrude","SWEPT_FACE",FACE,{"disambiguationData":[OSD([subQ1,sQuery(id+"F1.wireOp",EDGE,"E16.left")])]})]}),makeQuery(id+"F8.opExtrude","SWEPT_FACE",FACE,{"disambiguationData":[OSD([subQ1,sQuery(id+"F1.wireOp",EDGE,"E16.right")])]})]}),makeQuery(id+"F12.opExtrude","SWEPT_FACE",FACE,{"disambiguationData":[OSD([sQuery(id+"F11.wireOp",EDGE,"E26")])]})]}),makeQuery(id+"F14.opExtrude","SWEPT_FACE",FACE,{"disambiguationData":[OSD([subQ0,sQuery(id+"F13.wireOp",EDGE,"E30.0")])]})]})]});}
            var Q17;
            {var subQ0=sQuery(id+"F11.wireOp",EDGE,"E26");var subQ1=sQuery(id+"F1.wireOp",EDGE,"E16.top");Q17=makeQuery(id+"F15.opChamfer","BLEND_EDGE",EDGE,{"blendedFrom":[makeQuery(id+"F12.opExtrude","SWEPT_EDGE",EDGE,{"disambiguationData":[OSD([sQuery(id+"F11.wireOp",EDGE,"E25.top"),subQ0])]}),makeQuery(id+"F14.boolean.opBoolean","MERGE",FACE,{"derivedFrom":[makeQuery(id+"F12.boolean.opBoolean","MERGE",FACE,{"derivedFrom":[makeQuery(id+"F8.boolean.opBoolean","MERGE",FACE,{"derivedFrom":[makeQuery(id+"F7.boolean.opBoolean","MERGE",FACE,{"derivedFrom":[makeQuery(id+"F2.opExtrude","SWEPT_FACE",FACE,{"disambiguationData":[OSD([subQ1])]}),makeQuery(id+"F7.opExtrude","SWEPT_FACE",FACE,{"disambiguationData":[OSD([subQ1,sQuery(id+"F1.wireOp",EDGE,"E16.left")])]})]}),makeQuery(id+"F8.opExtrude","SWEPT_FACE",FACE,{"disambiguationData":[OSD([subQ1,sQuery(id+"F1.wireOp",EDGE,"E16.right")])]})]}),makeQuery(id+"F12.opExtrude","SWEPT_FACE",FACE,{"disambiguationData":[OSD([subQ0])]})]}),makeQuery(id+"F14.opExtrude","SWEPT_FACE",FACE,{"disambiguationData":[OSD([sQuery(id+"F13.wireOp",EDGE,"E27.0"),sQuery(id+"F13.wireOp",EDGE,"E30.0")])]})]})],"blendedInto":[makeQuery(id+"F14.boolean.opBoolean","MERGE",FACE,{"derivedFrom":[makeQuery(id+"F12.boolean.opBoolean","MERGE",FACE,{"derivedFrom":[makeQuery(id+"F8.boolean.opBoolean","MERGE",FACE,{"derivedFrom":[makeQuery(id+"F7.boolean.opBoolean","MERGE",FACE,{"derivedFrom":[makeQuery(id+"F2.opExtrude","SWEPT_FACE",FACE,{"disambiguationData":[OSD([subQ1])]}),makeQuery(id+"F7.opExtrude","SWEPT_FACE",FACE,{"disambiguationData":[OSD([subQ1,sQuery(id+"F1.wireOp",EDGE,"E16.left")])]})]}),makeQuery(id+"F8.opExtrude","SWEPT_FACE",FACE,{"disambiguationData":[OSD([subQ1,sQuery(id+"F1.wireOp",EDGE,"E16.right")])]})]}),makeQuery(id+"F12.opExtrude","SWEPT_FACE",FACE,{"disambiguationData":[OSD([subQ0])]})]}),makeQuery(id+"F14.opExtrude","SWEPT_FACE",FACE,{"disambiguationData":[OSD([sQuery(id+"F13.wireOp",EDGE,"E27.0"),sQuery(id+"F13.wireOp",EDGE,"E30.0")])]})]})]});}
            var Q18;
            {var subQ0=sQuery(id+"F13.wireOp",EDGE,"E28.0");Q18=makeQuery(id+"F15.opChamfer","BLEND_EDGE",EDGE,{"blendedFrom":[makeQuery(id+"F14.opExtrude","SWEPT_EDGE",EDGE,{"disambiguationData":[OSD([subQ0,sQuery(id+"F13.wireOp",EDGE,"E29.0")])]}),makeQuery(id+"F14.opExtrude","SWEPT_FACE",FACE,{"disambiguationData":[OSD([subQ0])]})],"blendedInto":[makeQuery(id+"F14.opExtrude","SWEPT_FACE",FACE,{"disambiguationData":[OSD([subQ0])]})]});}
            fillet(context, id + "F27", {"entities" : qUnion([Q0, Q1, Q2, Q3, Q4, Q5, Q6, Q7, Q8, Q9, Q10, Q11, Q12, Q13, Q14, Q15, Q16, Q17, Q18]), "radius" : 2 * mm, "tangentPropagation" : true, "allowEdgeOverflow" : false});
        }
        {
            var Q0;
            Q0=makeQuery(id+"F26.opExtrude","CAP_EDGE",EDGE,{"disambiguationData":[OSD([sQuery(id+"F25.wireOp",EDGE,"E62.bottom")])],"isStart":false});
            var Q1;
            Q1=makeQuery(id+"F26.opExtrude","CAP_EDGE",EDGE,{"disambiguationData":[OSD([sQuery(id+"F25.wireOp",EDGE,"E62.bottom")])],"isStart":true});
            fillet(context, id + "F28", {"entities" : qUnion([Q0, Q1]), "radius" : 1 * mm, "tangentPropagation" : true, "allowEdgeOverflow" : false});
        }
    });
